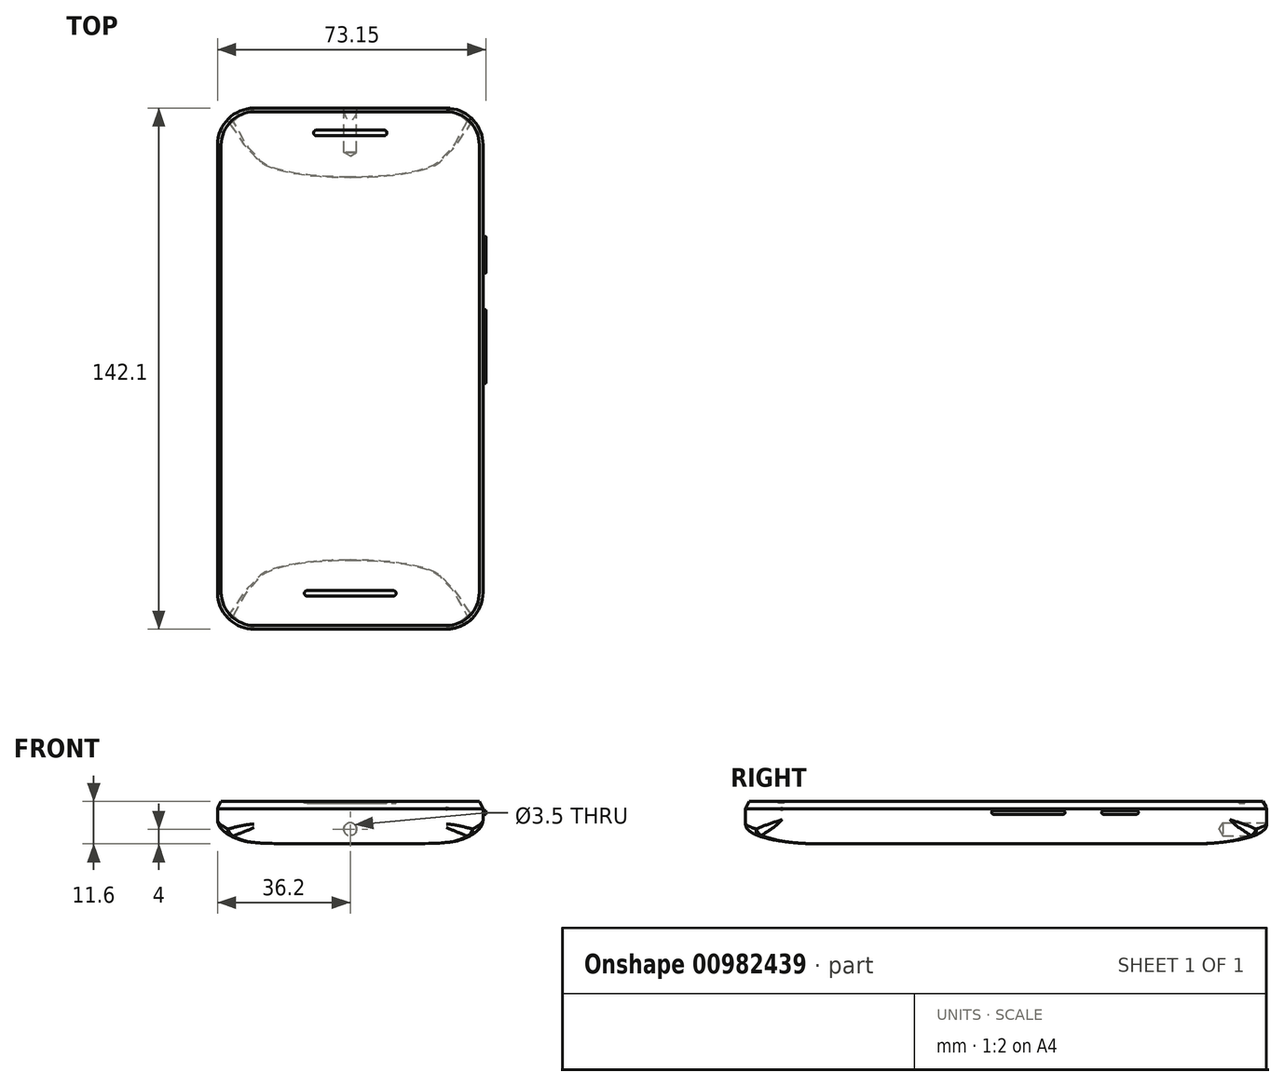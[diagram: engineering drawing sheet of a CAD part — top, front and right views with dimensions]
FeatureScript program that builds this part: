
annotation { "Feature Type Name" : "Feature", "Feature Type Description" : "" }
export const myFeature = defineFeature(function(context is Context, id is Id, definition is map)
    precondition{}
    {
        {
            var Q0;
            Q0=qCreatedBy(makeId("Top.planeOp"),FACE);
            var sketch = newSketch(context, id + "F0", { "sketchPlane" : qUnion([Q0])});
            skLineSegment(sketch, "E0.bottom", {"start": v(36.2, 71.05) * mm, "end": v(-36.2, 71.05) * mm});
            skLineSegment(sketch, "E0.top", {"start": v(36.2, -71.05) * mm, "end": v(-36.2, -71.05) * mm});
            skLineSegment(sketch, "E0.left", {"start": v(36.2, 71.05) * mm, "end": v(36.2, -71.05) * mm});
            skLineSegment(sketch, "E0.right", {"start": v(-36.2, 71.05) * mm, "end": v(-36.2, -71.05) * mm});
            skPoint(sketch, "E0.middle", {"position": v(0, 0) * mm});
            skSolve(sketch);
        }
        {
            var Q0;
            Q0=makeQuery(id+"F0.imprint","IMPRINT",FACE,{"disambiguationData":[TD([[makeQuery(id+"F0.imprint","IMPRINT",EDGE,{"derivedFrom":sQuery(id+"F0.wireOp",EDGE,"E0.bottom")}),1.0]])]});
            extrude(context, id + "F1", {"entities" : qUnion([Q0]), "depth" : 11.6 * mm, "offsetDistance" : 25 * mm});
        }
        {
            var Q0;
            Q0=makeQuery(id+"F1.opExtrude","SWEPT_EDGE",EDGE,{"disambiguationData":[OSD([sQuery(id+"F0.wireOp",EDGE,"E0.bottom"),sQuery(id+"F0.wireOp",EDGE,"E0.right")])]});
            var Q1;
            Q1=makeQuery(id+"F1.opExtrude","SWEPT_EDGE",EDGE,{"disambiguationData":[OSD([sQuery(id+"F0.wireOp",EDGE,"E0.top"),sQuery(id+"F0.wireOp",EDGE,"E0.right")])]});
            var Q2;
            Q2=makeQuery(id+"F1.opExtrude","SWEPT_EDGE",EDGE,{"disambiguationData":[OSD([sQuery(id+"F0.wireOp",EDGE,"E0.top"),sQuery(id+"F0.wireOp",EDGE,"E0.left")])]});
            var Q3;
            Q3=makeQuery(id+"F1.opExtrude","SWEPT_EDGE",EDGE,{"disambiguationData":[OSD([sQuery(id+"F0.wireOp",EDGE,"E0.bottom"),sQuery(id+"F0.wireOp",EDGE,"E0.left")])]});
            fillet(context, id + "F2", {"entities" : qUnion([Q0, Q1, Q2, Q3]), "radius" : 10 * mm, "tangentPropagation" : true, "allowEdgeOverflow" : false});
        }
        {
            var Q0;
            Q0=makeQuery(id+"F1.opExtrude","CAP_EDGE",EDGE,{"disambiguationData":[OSD([sQuery(id+"F0.wireOp",EDGE,"E0.right")])],"isStart":false});
            chamfer(context, id + "F3", {"entities" : qUnion([Q0]), "chamferType" : ChamferType.TWO_OFFSETS, "width1" : 1 * mm, "oppositeDirection" : false, "width2" : 2 * mm, "tangentPropagation" : true});
        }
        {
            var Q0;
            Q0=makeQuery(id+"F1.opExtrude","SWEPT_FACE",FACE,{"disambiguationData":[OSD([sQuery(id+"F0.wireOp",EDGE,"E0.bottom")])]});
            var sketch = newSketch(context, id + "F4", { "sketchPlane" : qUnion([Q0])});
            skLineSegment(sketch, "E1.0", {"start": v(-36.2, 0) * mm, "end": v(-36.2, 9.6) * mm, "construction": true});
            skLineSegment(sketch, "E1.1", {"start": v(36.2, 9.6) * mm, "end": v(36.2, 0) * mm, "construction": true});
            skLineSegment(sketch, "E2", {"start": v(-36.2, 9.6) * mm, "end": v(-36.2, 6.6) * mm});
            skLineSegment(sketch, "E3", {"start": v(-36.2, 6.6) * mm, "end": v(-36.2, 0) * mm});
            skLineSegment(sketch, "E4", {"start": v(-36.2, 0) * mm, "end": v(36.2, 0) * mm});
            skLineSegment(sketch, "E5", {"start": v(36.2, 0) * mm, "end": v(36.2, 6.6) * mm});
            skFitSpline(sketch, "E6", {"points": [v(-36.2, 6.6) * mm, v(-30, 1.1) * mm, v(-26.2, 0.4) * mm, v(0, 0) * mm], "startDerivative": vector(0, -28.8) * mm, "endDerivative": vector(153, 0) * mm});
            skLineSegment(sketch, "E7", {"start": v(0, 0) * mm, "end": v(0, 9.6) * mm, "construction": true});
            skFitSpline(sketch, "E8.MirrorCS", {"points": [v(36.2, 6.6) * mm, v(30, 1.1) * mm, v(26.2, 0.4) * mm, v(0, 0) * mm], "startDerivative": vector(0, -28.8) * mm, "endDerivative": vector(-153, 0) * mm});
            skSolve(sketch);
        }
        {
            var Q0;
            {var subQ0=sQuery(id+"F4.wireOp",EDGE,"E3");Q0=makeQuery(id+"F4.imprint","IMPRINT",FACE,{"disambiguationData":[TD([[makeQuery(id+"F4.imprint","IMPRINT",EDGE,{"derivedFrom":subQ0}),1.0]])]});}
            var Q1;
            {var subQ0=sQuery(id+"F4.wireOp",EDGE,"E4");var subQ4=sQuery(id+"F4.wireOp",EDGE,"E6");var subQ5=makeQuery(id+"F4.imprint","INTERSECT",VERTEX,{"derivedFrom":[subQ0,subQ4,sQuery(id+"F4.wireOp",EDGE,"E8.MirrorCS")]});Q1=makeQuery(id+"F4.imprint","IMPRINT",FACE,{"disambiguationData":[TD([[makeQuery(id+"F4.imprint","IMPRINT",EDGE,{"disambiguationData":[TD([[subQ5,1.0]])],"derivedFrom":subQ0}),1.0]])]});}
            var Q2;
            {var subQ4=sQuery(id+"F4.wireOp",EDGE,"E5");Q2=makeQuery(id+"F4.imprint","IMPRINT",FACE,{"disambiguationData":[TD([[makeQuery(id+"F4.imprint","IMPRINT",EDGE,{"derivedFrom":subQ4}),1.0]])]});}
            var Q3;
            {var subQ0=sQuery(id+"F4.wireOp",EDGE,"E4");var subQ4=sQuery(id+"F4.wireOp",EDGE,"E8.MirrorCS");var subQ5=makeQuery(id+"F4.imprint","INTERSECT",VERTEX,{"derivedFrom":[subQ0,sQuery(id+"F4.wireOp",EDGE,"E6"),subQ4]});Q3=makeQuery(id+"F4.imprint","IMPRINT",FACE,{"disambiguationData":[TD([[makeQuery(id+"F4.imprint","IMPRINT",EDGE,{"disambiguationData":[TD([[subQ5,-1.0]])],"derivedFrom":subQ0}),1.0]])]});}
            extrude(context, id + "F5", {"entities" : qUnion([Q0, Q1, Q2, Q3]), "operationType" : NewBodyOperationType.REMOVE, "endBound" : BoundingType.THROUGH_ALL, "oppositeDirection" : true, "depth" : 25 * mm, "offsetDistance" : 25 * mm});
        }
        {
            var Q0;
            Q0=makeQuery(id+"F1.opExtrude","SWEPT_FACE",FACE,{"disambiguationData":[OSD([sQuery(id+"F0.wireOp",EDGE,"E0.left")])]});
            var sketch = newSketch(context, id + "F6", { "sketchPlane" : qUnion([Q0])});
            skLineSegment(sketch, "E9.bottom", {"start": v(36.05, 9.1) * mm, "end": v(26.05, 9.1) * mm});
            skLineSegment(sketch, "E9.top", {"start": v(36.05, 8.1) * mm, "end": v(26.05, 8.1) * mm});
            skLineSegment(sketch, "E9.left", {"start": v(26.05, 9.1) * mm, "end": v(26.05, 8.1) * mm});
            skLineSegment(sketch, "E9.right", {"start": v(36.05, 9.1) * mm, "end": v(36.05, 8.1) * mm});
            skLineSegment(sketch, "E10.bottom", {"start": v(16.05, 9.1) * mm, "end": v(-3.95, 9.1) * mm});
            skLineSegment(sketch, "E10.top", {"start": v(16.05, 8.1) * mm, "end": v(-3.95, 8.1) * mm});
            skLineSegment(sketch, "E10.left", {"start": v(16.05, 9.1) * mm, "end": v(16.05, 8.1) * mm});
            skLineSegment(sketch, "E10.right", {"start": v(-3.95, 9.1) * mm, "end": v(-3.95, 8.1) * mm});
            skSolve(sketch);
        }
        {
            var Q0;
            Q0=makeQuery(id+"F6.imprint","IMPRINT",FACE,{"disambiguationData":[TD([[makeQuery(id+"F6.imprint","IMPRINT",EDGE,{"derivedFrom":sQuery(id+"F6.wireOp",EDGE,"E10.bottom")}),1.0]])]});
            var Q1;
            Q1=makeQuery(id+"F6.imprint","IMPRINT",FACE,{"disambiguationData":[TD([[makeQuery(id+"F6.imprint","IMPRINT",EDGE,{"derivedFrom":sQuery(id+"F6.wireOp",EDGE,"E9.bottom")}),1.0]])]});
            extrude(context, id + "F7", {"entities" : qUnion([Q0, Q1]), "operationType" : NewBodyOperationType.ADD, "depth" : 0.75 * mm, "offsetDistance" : 25 * mm});
        }
        {
            var Q0;
            Q0=makeQuery(id+"F7.opExtrude","SWEPT_EDGE",EDGE,{"disambiguationData":[OSD([sQuery(id+"F6.wireOp",EDGE,"E10.bottom"),sQuery(id+"F6.wireOp",EDGE,"E10.right")])]});
            var Q1;
            Q1=makeQuery(id+"F7.opExtrude","SWEPT_EDGE",EDGE,{"disambiguationData":[OSD([sQuery(id+"F6.wireOp",EDGE,"E10.top"),sQuery(id+"F6.wireOp",EDGE,"E10.right")])]});
            var Q2;
            Q2=makeQuery(id+"F7.opExtrude","SWEPT_EDGE",EDGE,{"disambiguationData":[OSD([sQuery(id+"F6.wireOp",EDGE,"E10.top"),sQuery(id+"F6.wireOp",EDGE,"E10.left")])]});
            var Q3;
            Q3=makeQuery(id+"F7.opExtrude","SWEPT_EDGE",EDGE,{"disambiguationData":[OSD([sQuery(id+"F6.wireOp",EDGE,"E10.bottom"),sQuery(id+"F6.wireOp",EDGE,"E10.left")])]});
            var Q4;
            Q4=makeQuery(id+"F7.opExtrude","SWEPT_EDGE",EDGE,{"disambiguationData":[OSD([sQuery(id+"F6.wireOp",EDGE,"E9.bottom"),sQuery(id+"F6.wireOp",EDGE,"E9.left")])]});
            var Q5;
            Q5=makeQuery(id+"F7.opExtrude","SWEPT_EDGE",EDGE,{"disambiguationData":[OSD([sQuery(id+"F6.wireOp",EDGE,"E9.top"),sQuery(id+"F6.wireOp",EDGE,"E9.left")])]});
            var Q6;
            Q6=makeQuery(id+"F7.opExtrude","SWEPT_EDGE",EDGE,{"disambiguationData":[OSD([sQuery(id+"F6.wireOp",EDGE,"E9.top"),sQuery(id+"F6.wireOp",EDGE,"E9.right")])]});
            var Q7;
            Q7=makeQuery(id+"F7.opExtrude","SWEPT_EDGE",EDGE,{"disambiguationData":[OSD([sQuery(id+"F6.wireOp",EDGE,"E9.bottom"),sQuery(id+"F6.wireOp",EDGE,"E9.right")])]});
            fillet(context, id + "F8", {"entities" : qUnion([Q0, Q1, Q2, Q3, Q4, Q5, Q6, Q7]), "radius" : 0.5 * mm, "tangentPropagation" : true, "allowEdgeOverflow" : false});
        }
        {
            var Q0;
            Q0=makeQuery(id+"F1.opExtrude","SWEPT_FACE",FACE,{"disambiguationData":[OSD([sQuery(id+"F0.wireOp",EDGE,"E0.bottom")])]});
            var sketch = newSketch(context, id + "F9", { "sketchPlane" : qUnion([Q0])});
            skLineSegment(sketch, "E11", {"start": v(0, 9.6) * mm, "end": v(0, 0) * mm});
            skPoint(sketch, "E12", {"position": v(0, 4) * mm});
            skSolve(sketch);
        }
        {
            var Q0;
            Q0=sQuery(id+"F9.wireOp",VERTEX,"E12");
            var Q1;
            Q1=makeQuery(id+"F1.opExtrude","SWEPT_BODY",BODY,{"disambiguationData":[OSD([sQuery(id+"F0.wireOp",EDGE,"E0.bottom"),sQuery(id+"F0.wireOp",EDGE,"E0.top"),sQuery(id+"F0.wireOp",EDGE,"E0.left"),sQuery(id+"F0.wireOp",EDGE,"E0.right")])]});
            hole(context, id + "F10", {"style" : HoleStyle.SIMPLE, "endStyle" : HoleEndStyle.BLIND, "holeDiameter" : 3.5 * mm, "majorDiameter" : 7.94 * mm, "holeDepth" : 12 * mm, "isTappedThrough" : true, "tappedDepth" : 7.77 * mm, "tapClearance" : 3, "locations" : qUnion([Q0]), "scope" : qUnion([Q1])});
        }
        {
            var Q0;
            Q0=makeQuery(id+"F1.opExtrude","SWEPT_FACE",FACE,{"disambiguationData":[OSD([sQuery(id+"F0.wireOp",EDGE,"E0.right")])]});
            var sketch = newSketch(context, id + "F11", { "sketchPlane" : qUnion([Q0])});
            skLineSegment(sketch, "E13.0", {"start": v(-71.05, 0.4) * mm, "end": v(-71.05, 9.6) * mm, "construction": true});
            skLineSegment(sketch, "E13.1", {"start": v(71.05, 9.6) * mm, "end": v(71.05, 0.4) * mm, "construction": true});
            skLineSegment(sketch, "E14", {"start": v(-71.05, 0.4) * mm, "end": v(-71.05, 5.4) * mm});
            skLineSegment(sketch, "E15", {"start": v(71.05, 0.4) * mm, "end": v(71.05, 5.4) * mm});
            skFitSpline(sketch, "E16", {"points": [v(-71.05, 5.4) * mm, v(-61, 0.71) * mm, v(-36.74, 0) * mm], "startDerivative": vector(0, -18.6) * mm, "endDerivative": vector(41.89, 0) * mm});
            skLineSegment(sketch, "E17", {"start": v(0, 0) * mm, "end": v(0, 6.6) * mm, "construction": true});
            skFitSpline(sketch, "E18.0", {"points": [v(-71.05, 0.4) * mm, v(-71.05, 0.27) * mm, v(-71.05, 0.13) * mm, v(-71.05, 0) * mm]});
            skFitSpline(sketch, "E19.MirrorCS", {"points": [v(71.05, 0.4) * mm, v(71.05, 0.27) * mm, v(71.05, 0.13) * mm, v(71.05, 0) * mm]});
            skLineSegment(sketch, "E20", {"start": v(71.05, 0) * mm, "end": v(-71.05, 0) * mm});
            skFitSpline(sketch, "E21.MirrorCS", {"points": [v(71.05, 5.4) * mm, v(61, 0.71) * mm, v(36.74, 0) * mm], "startDerivative": vector(0, -18.6) * mm, "endDerivative": vector(-41.89, 0) * mm});
            skSolve(sketch);
        }
        {
            var Q0;
            {var subQ0=sQuery(id+"F11.wireOp",EDGE,"E14");Q0=makeQuery(id+"F11.imprint","IMPRINT",FACE,{"disambiguationData":[TD([[makeQuery(id+"F11.imprint","IMPRINT",EDGE,{"derivedFrom":subQ0}),-1.0]])]});}
            var Q1;
            {var subQ0=sQuery(id+"F11.wireOp",EDGE,"E15");Q1=makeQuery(id+"F11.imprint","IMPRINT",FACE,{"disambiguationData":[TD([[makeQuery(id+"F11.imprint","IMPRINT",EDGE,{"derivedFrom":subQ0}),1.0]])]});}
            extrude(context, id + "F12", {"entities" : qUnion([Q0, Q1]), "operationType" : NewBodyOperationType.REMOVE, "endBound" : BoundingType.THROUGH_ALL, "oppositeDirection" : true, "depth" : 25 * mm, "offsetDistance" : 25 * mm});
        }
        {
            var Q0;
            Q0=makeQuery(id+"F1.opExtrude","CAP_FACE",FACE,{"disambiguationData":[OSD([sQuery(id+"F0.wireOp",EDGE,"E0.bottom"),sQuery(id+"F0.wireOp",EDGE,"E0.top"),sQuery(id+"F0.wireOp",EDGE,"E0.left"),sQuery(id+"F0.wireOp",EDGE,"E0.right")])],"isStart":false});
            var sketch = newSketch(context, id + "F13", { "sketchPlane" : qUnion([Q0])});
            skLineSegment(sketch, "E22.bottom", {"start": v(-10, 65.05) * mm, "end": v(10, 65.05) * mm});
            skLineSegment(sketch, "E22.top", {"start": v(-10, 63.55) * mm, "end": v(10, 63.55) * mm});
            skLineSegment(sketch, "E22.left", {"start": v(-10, 65.05) * mm, "end": v(-10, 63.55) * mm});
            skLineSegment(sketch, "E22.right", {"start": v(10, 65.05) * mm, "end": v(10, 63.55) * mm});
            skPoint(sketch, "E22.middle", {"position": v(0, 64.3) * mm});
            skPoint(sketch, "E22.middle.positionSnap0", {"position": v(0, 70.05) * mm});
            skPoint(sketch, "E22.centerSnap0", {"position": v(0, 70.05) * mm});
            skLineSegment(sketch, "E23.bottom", {"start": v(-12.5, -60.55) * mm, "end": v(12.5, -60.55) * mm});
            skLineSegment(sketch, "E23.top", {"start": v(-12.5, -62.05) * mm, "end": v(12.5, -62.05) * mm});
            skLineSegment(sketch, "E23.left", {"start": v(-12.5, -60.55) * mm, "end": v(-12.5, -62.05) * mm});
            skLineSegment(sketch, "E23.right", {"start": v(12.5, -60.55) * mm, "end": v(12.5, -62.05) * mm});
            skPoint(sketch, "E23.middle", {"position": v(0, -61.3) * mm});
            skPoint(sketch, "E23.middle.positionSnap0", {"position": v(0, -70.05) * mm});
            skPoint(sketch, "E23.centerSnap0", {"position": v(0, -70.05) * mm});
            skSolve(sketch);
        }
        {
            var Q0;
            Q0=makeQuery(id+"F13.imprint","IMPRINT",FACE,{"disambiguationData":[TD([[makeQuery(id+"F13.imprint","IMPRINT",EDGE,{"derivedFrom":sQuery(id+"F13.wireOp",EDGE,"E23.bottom")}),-1.0]])]});
            var Q1;
            Q1=makeQuery(id+"F13.imprint","IMPRINT",FACE,{"disambiguationData":[TD([[makeQuery(id+"F13.imprint","IMPRINT",EDGE,{"derivedFrom":sQuery(id+"F13.wireOp",EDGE,"E22.bottom")}),-1.0]])]});
            extrude(context, id + "F14", {"entities" : qUnion([Q0, Q1]), "operationType" : NewBodyOperationType.REMOVE, "oppositeDirection" : true, "depth" : 0.5 * mm, "offsetDistance" : 25 * mm});
        }
        {
            var Q0;
            Q0=makeQuery(id+"F14.boolean.opBoolean","COPY",EDGE,{"derivedFrom":makeQuery(id+"F14.opExtrude","SWEPT_EDGE",EDGE,{"disambiguationData":[OSD([sQuery(id+"F13.wireOp",EDGE,"E22.bottom"),sQuery(id+"F13.wireOp",EDGE,"E22.left")])]})});
            var Q1;
            Q1=makeQuery(id+"F14.boolean.opBoolean","COPY",EDGE,{"derivedFrom":makeQuery(id+"F14.opExtrude","SWEPT_EDGE",EDGE,{"disambiguationData":[OSD([sQuery(id+"F13.wireOp",EDGE,"E22.top"),sQuery(id+"F13.wireOp",EDGE,"E22.left")])]})});
            var Q2;
            Q2=makeQuery(id+"F14.boolean.opBoolean","COPY",EDGE,{"derivedFrom":makeQuery(id+"F14.opExtrude","SWEPT_EDGE",EDGE,{"disambiguationData":[OSD([sQuery(id+"F13.wireOp",EDGE,"E22.bottom"),sQuery(id+"F13.wireOp",EDGE,"E22.right")])]})});
            var Q3;
            Q3=makeQuery(id+"F14.boolean.opBoolean","COPY",EDGE,{"derivedFrom":makeQuery(id+"F14.opExtrude","SWEPT_EDGE",EDGE,{"disambiguationData":[OSD([sQuery(id+"F13.wireOp",EDGE,"E22.top"),sQuery(id+"F13.wireOp",EDGE,"E22.right")])]})});
            var Q4;
            Q4=makeQuery(id+"F14.boolean.opBoolean","COPY",EDGE,{"derivedFrom":makeQuery(id+"F14.opExtrude","SWEPT_EDGE",EDGE,{"disambiguationData":[OSD([sQuery(id+"F13.wireOp",EDGE,"E23.top"),sQuery(id+"F13.wireOp",EDGE,"E23.right")])]})});
            var Q5;
            Q5=makeQuery(id+"F14.boolean.opBoolean","COPY",EDGE,{"derivedFrom":makeQuery(id+"F14.opExtrude","SWEPT_EDGE",EDGE,{"disambiguationData":[OSD([sQuery(id+"F13.wireOp",EDGE,"E23.bottom"),sQuery(id+"F13.wireOp",EDGE,"E23.right")])]})});
            var Q6;
            Q6=makeQuery(id+"F14.boolean.opBoolean","COPY",EDGE,{"derivedFrom":makeQuery(id+"F14.opExtrude","SWEPT_EDGE",EDGE,{"disambiguationData":[OSD([sQuery(id+"F13.wireOp",EDGE,"E23.bottom"),sQuery(id+"F13.wireOp",EDGE,"E23.left")])]})});
            var Q7;
            Q7=makeQuery(id+"F14.boolean.opBoolean","COPY",EDGE,{"derivedFrom":makeQuery(id+"F14.opExtrude","SWEPT_EDGE",EDGE,{"disambiguationData":[OSD([sQuery(id+"F13.wireOp",EDGE,"E23.top"),sQuery(id+"F13.wireOp",EDGE,"E23.left")])]})});
            fillet(context, id + "F15", {"entities" : qUnion([Q0, Q1, Q2, Q3, Q4, Q5, Q6, Q7]), "radius" : 0.75 * mm, "allowEdgeOverflow" : false});
        }
        {
            var Q0;
            Q0=makeQuery(id+"F5.boolean.opBoolean","INTERSECT",EDGE,{"derivedFrom":[makeQuery(id+"F2.opFillet","BLEND_FACE",FACE,{"disambiguationData":[OSD([sQuery(id+"F0.wireOp",EDGE,"E0.bottom"),sQuery(id+"F0.wireOp",EDGE,"E0.right")])]}),makeQuery(id+"F5.opExtrude","SWEPT_FACE",FACE,{"disambiguationData":[OSD([sQuery(id+"F4.wireOp",EDGE,"E8.MirrorCS")])]})]});
            var Q1;
            {var subQ0=sQuery(id+"F0.wireOp",EDGE,"E0.right");Q1=makeQuery(id+"F2.opFillet","BLEND_EDGE",EDGE,{"blendedFrom":[makeQuery(id+"F1.opExtrude","SWEPT_EDGE",EDGE,{"disambiguationData":[OSD([sQuery(id+"F0.wireOp",EDGE,"E0.bottom"),subQ0])]}),makeQuery(id+"F1.opExtrude","SWEPT_FACE",FACE,{"disambiguationData":[OSD([subQ0])]})],"blendedInto":[makeQuery(id+"F1.opExtrude","SWEPT_FACE",FACE,{"disambiguationData":[OSD([subQ0])]})]});}
            var Q2;
            Q2=makeQuery(id+"F2.opFillet","BLEND_FACE",FACE,{"disambiguationData":[OSD([sQuery(id+"F0.wireOp",EDGE,"E0.bottom"),sQuery(id+"F0.wireOp",EDGE,"E0.right")])]});
            var Q3;
            Q3=makeQuery(id+"F12.boolean.opBoolean","INTERSECT",EDGE,{"derivedFrom":[makeQuery(id+"F5.boolean.opBoolean","COPY",FACE,{"derivedFrom":makeQuery(id+"F5.opExtrude","SWEPT_FACE",FACE,{"disambiguationData":[OSD([sQuery(id+"F4.wireOp",EDGE,"E8.MirrorCS")])]})}),makeQuery(id+"F12.opExtrude","SWEPT_FACE",FACE,{"disambiguationData":[OSD([sQuery(id+"F11.wireOp",EDGE,"E16")])]})]});
            var Q4;
            Q4=makeQuery(id+"F12.boolean.opBoolean","INTERSECT",EDGE,{"derivedFrom":[makeQuery(id+"F5.boolean.opBoolean","COPY",FACE,{"derivedFrom":makeQuery(id+"F5.opExtrude","SWEPT_FACE",FACE,{"disambiguationData":[OSD([sQuery(id+"F4.wireOp",EDGE,"E6")])]})}),makeQuery(id+"F12.opExtrude","SWEPT_FACE",FACE,{"disambiguationData":[OSD([sQuery(id+"F11.wireOp",EDGE,"E16")])]})]});
            var Q5;
            Q5=makeQuery(id+"F5.boolean.opBoolean","INTERSECT",EDGE,{"derivedFrom":[makeQuery(id+"F2.opFillet","BLEND_FACE",FACE,{"disambiguationData":[OSD([sQuery(id+"F0.wireOp",EDGE,"E0.bottom"),sQuery(id+"F0.wireOp",EDGE,"E0.left")])]}),makeQuery(id+"F5.opExtrude","SWEPT_FACE",FACE,{"disambiguationData":[OSD([sQuery(id+"F4.wireOp",EDGE,"E6")])]})]});
            var Q6;
            Q6=makeQuery(id+"F12.boolean.opBoolean","INTERSECT",EDGE,{"derivedFrom":[makeQuery(id+"F2.opFillet","BLEND_FACE",FACE,{"disambiguationData":[OSD([sQuery(id+"F0.wireOp",EDGE,"E0.bottom"),sQuery(id+"F0.wireOp",EDGE,"E0.left")])]}),makeQuery(id+"F12.opExtrude","SWEPT_FACE",FACE,{"disambiguationData":[OSD([sQuery(id+"F11.wireOp",EDGE,"E16")])]})]});
            var Q7;
            Q7=makeQuery(id+"F12.boolean.opBoolean","INTERSECT",EDGE,{"derivedFrom":[makeQuery(id+"F2.opFillet","BLEND_FACE",FACE,{"disambiguationData":[OSD([sQuery(id+"F0.wireOp",EDGE,"E0.top"),sQuery(id+"F0.wireOp",EDGE,"E0.right")])]}),makeQuery(id+"F12.opExtrude","SWEPT_FACE",FACE,{"disambiguationData":[OSD([sQuery(id+"F11.wireOp",EDGE,"E21.MirrorCS")])]})]});
            var Q8;
            Q8=makeQuery(id+"F5.boolean.opBoolean","INTERSECT",EDGE,{"derivedFrom":[makeQuery(id+"F2.opFillet","BLEND_FACE",FACE,{"disambiguationData":[OSD([sQuery(id+"F0.wireOp",EDGE,"E0.top"),sQuery(id+"F0.wireOp",EDGE,"E0.right")])]}),makeQuery(id+"F5.opExtrude","SWEPT_FACE",FACE,{"disambiguationData":[OSD([sQuery(id+"F4.wireOp",EDGE,"E8.MirrorCS")])]})]});
            var Q9;
            Q9=makeQuery(id+"F12.boolean.opBoolean","INTERSECT",EDGE,{"derivedFrom":[makeQuery(id+"F5.boolean.opBoolean","COPY",FACE,{"derivedFrom":makeQuery(id+"F5.opExtrude","SWEPT_FACE",FACE,{"disambiguationData":[OSD([sQuery(id+"F4.wireOp",EDGE,"E8.MirrorCS")])]})}),makeQuery(id+"F12.opExtrude","SWEPT_FACE",FACE,{"disambiguationData":[OSD([sQuery(id+"F11.wireOp",EDGE,"E21.MirrorCS")])]})]});
            var Q10;
            Q10=makeQuery(id+"F12.boolean.opBoolean","INTERSECT",EDGE,{"derivedFrom":[makeQuery(id+"F5.boolean.opBoolean","COPY",FACE,{"derivedFrom":makeQuery(id+"F5.opExtrude","SWEPT_FACE",FACE,{"disambiguationData":[OSD([sQuery(id+"F4.wireOp",EDGE,"E6")])]})}),makeQuery(id+"F12.opExtrude","SWEPT_FACE",FACE,{"disambiguationData":[OSD([sQuery(id+"F11.wireOp",EDGE,"E21.MirrorCS")])]})]});
            var Q11;
            Q11=makeQuery(id+"F12.boolean.opBoolean","INTERSECT",EDGE,{"derivedFrom":[makeQuery(id+"F2.opFillet","BLEND_FACE",FACE,{"disambiguationData":[OSD([sQuery(id+"F0.wireOp",EDGE,"E0.top"),sQuery(id+"F0.wireOp",EDGE,"E0.left")])]}),makeQuery(id+"F12.opExtrude","SWEPT_FACE",FACE,{"disambiguationData":[OSD([sQuery(id+"F11.wireOp",EDGE,"E21.MirrorCS")])]})]});
            var Q12;
            Q12=makeQuery(id+"F5.boolean.opBoolean","INTERSECT",EDGE,{"derivedFrom":[makeQuery(id+"F2.opFillet","BLEND_FACE",FACE,{"disambiguationData":[OSD([sQuery(id+"F0.wireOp",EDGE,"E0.top"),sQuery(id+"F0.wireOp",EDGE,"E0.left")])]}),makeQuery(id+"F5.opExtrude","SWEPT_FACE",FACE,{"disambiguationData":[OSD([sQuery(id+"F4.wireOp",EDGE,"E6")])]})]});
            fillet(context, id + "F16", {"entities" : qUnion([Q0, Q1, Q2, Q3, Q4, Q5, Q6, Q7, Q8, Q9, Q10, Q11, Q12]), "radius" : (2) * mm, "allowEdgeOverflow" : false});
        }
    });
